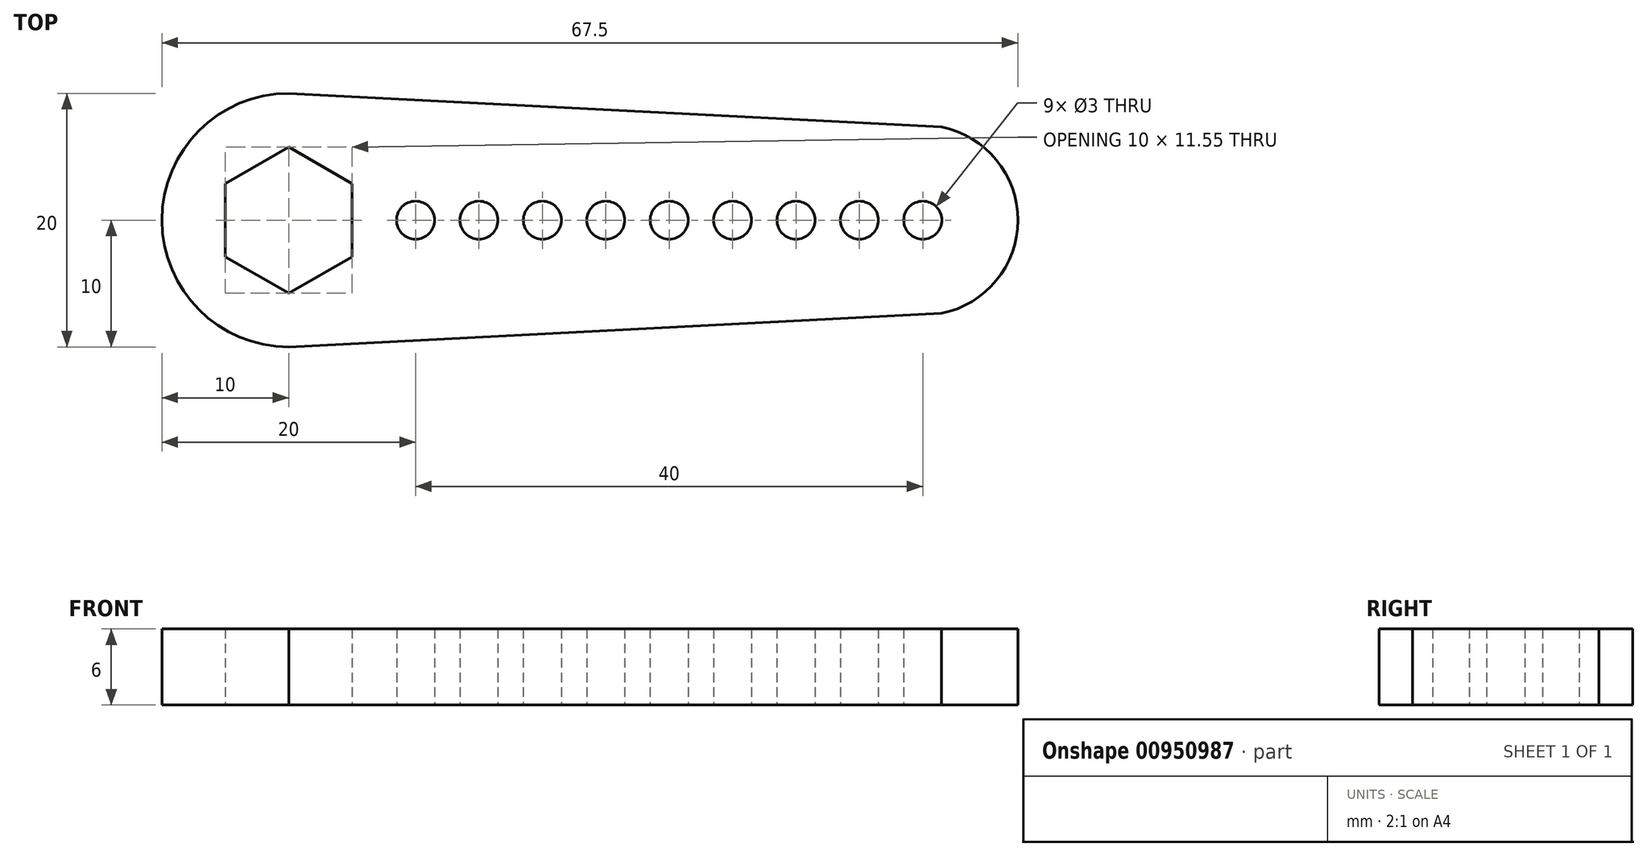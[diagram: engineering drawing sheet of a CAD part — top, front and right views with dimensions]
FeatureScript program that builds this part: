
annotation { "Feature Type Name" : "Feature", "Feature Type Description" : "" }
export const myFeature = defineFeature(function(context is Context, id is Id, definition is map)
    precondition{}
    {
        {
            var Q0;
            Q0=qCreatedBy(makeId("Top.planeOp"),FACE);
            var sketch = newSketch(context, id + "F0", { "sketchPlane" : qUnion([Q0])});
            skCircle(sketch, "E0.cCircle", {"center": v(0, 0) * mm, "radius": 5.77 * mm, "construction": true});
            skLineSegment(sketch, "E0.0", {"start": v(0, 5.77) * mm, "end": v(5, 2.89) * mm});
            skLineSegment(sketch, "E0.1", {"start": v(5, 2.89) * mm, "end": v(5, -2.89) * mm});
            skLineSegment(sketch, "E0.2", {"start": v(5, -2.89) * mm, "end": v(0, -5.77) * mm});
            skLineSegment(sketch, "E0.3", {"start": v(0, -5.77) * mm, "end": v(-5, -2.89) * mm});
            skLineSegment(sketch, "E0.4", {"start": v(-5, -2.89) * mm, "end": v(-5, 2.89) * mm});
            skLineSegment(sketch, "E0.5", {"start": v(-5, 2.89) * mm, "end": v(0, 5.77) * mm});
            skArc(sketch, "E1", {"start": v(0, 10) * mm, "mid": v(-10, 0) * mm, "end": v(0, -10) * mm});
            skArc(sketch, "E2", {"start": v(51.47, -7.36) * mm, "mid": v(57.5, 0) * mm, "end": v(51.47, 7.36) * mm});
            skLineSegment(sketch, "E3", {"start": v(51.47, 7.36) * mm, "end": v(0, 10) * mm});
            skCircle(sketch, "E4", {"center": v(10, 0) * mm, "radius": 1.5 * mm});
            skLineSegment(sketch, "E5.MirrorCS", {"start": v(51.47, -7.36) * mm, "end": v(0, -10) * mm});
            skCircle(sketch, "E6.1.0.0", {"center": v(15, 0) * mm, "radius": 1.5 * mm});
            skCircle(sketch, "E6.2.0.0", {"center": v(20, 0) * mm, "radius": 1.5 * mm});
            skCircle(sketch, "E6.3.0.0", {"center": v(25, 0) * mm, "radius": 1.5 * mm});
            skCircle(sketch, "E6.4.0.0", {"center": v(30, 0) * mm, "radius": 1.5 * mm});
            skCircle(sketch, "E6.5.0.0", {"center": v(35, 0) * mm, "radius": 1.5 * mm});
            skCircle(sketch, "E6.6.0.0", {"center": v(40, 0) * mm, "radius": 1.5 * mm});
            skCircle(sketch, "E6.7.0.0", {"center": v(45, 0) * mm, "radius": 1.5 * mm});
            skCircle(sketch, "E6.8.0.0", {"center": v(50, 0) * mm, "radius": 1.5 * mm});
            skLineSegment(sketch, "E6.direction1", {"start": v(10, 0) * mm, "end": v(15, 0) * mm, "construction": true});
            skSolve(sketch);
        }
        {
            var Q0;
            Q0=makeQuery(id+"F0.imprint","IMPRINT",FACE,{"disambiguationData":[TD([[makeQuery(id+"F0.imprint","IMPRINT",EDGE,{"derivedFrom":sQuery(id+"F0.wireOp",EDGE,"E0.0")}),1.0]])]});
            extrude(context, id + "F1", {"entities" : qUnion([Q0]), "depth" : 6 * mm, "offsetDistance" : 25 * mm});
        }
    });
